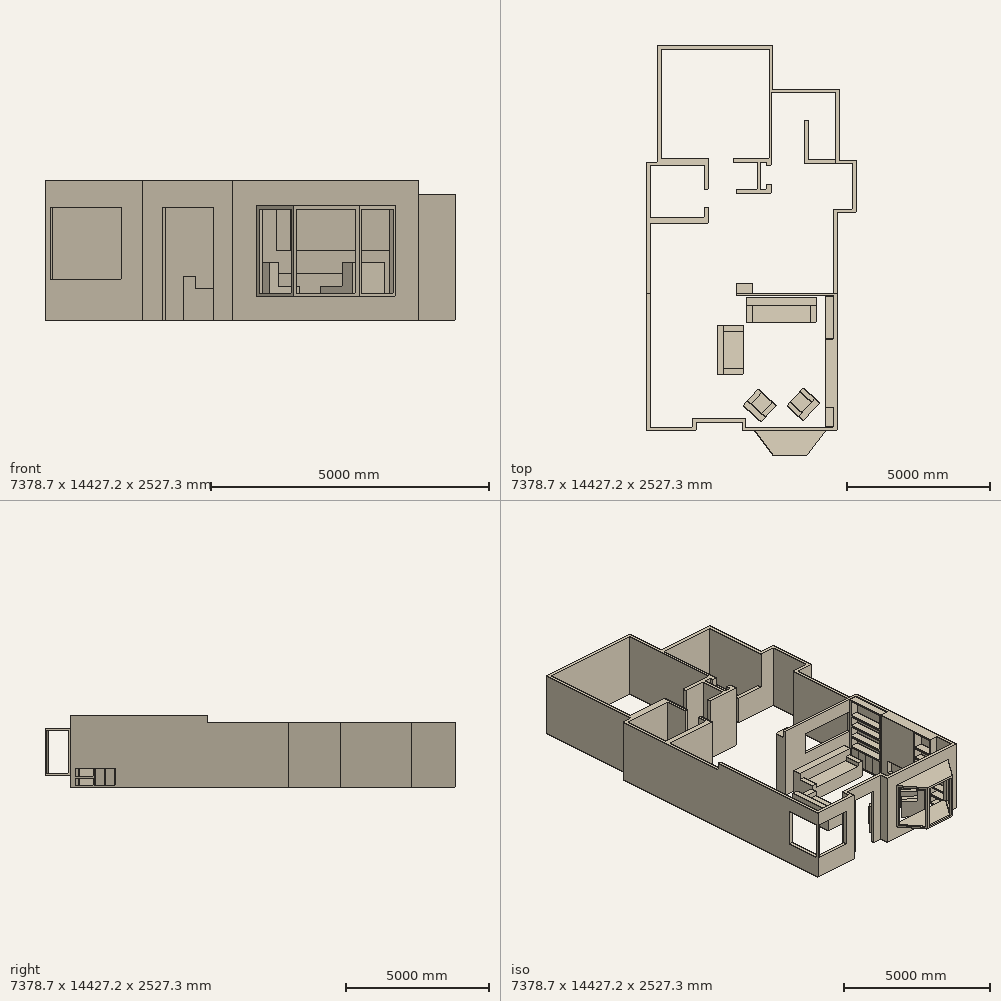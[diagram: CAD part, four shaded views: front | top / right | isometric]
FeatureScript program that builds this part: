
annotation { "Feature Type Name" : "Feature", "Feature Type Description" : "" }
export const myFeature = defineFeature(function(context is Context, id is Id, definition is map)
    precondition{}
    {
        {
            var Q0;
            Q0=qCreatedBy(makeId("Top.planeOp"),FACE);
            var sketch = newSketch(context, id + "F0", { "sketchPlane" : qUnion([Q0])});
            skLineSegment(sketch, "E0", {"start": v(6464.3, 0) * mm, "end": v(6464.3, 4622.8) * mm});
            skLineSegment(sketch, "E1", {"start": v(0, 0) * mm, "end": v(1498.6, 0) * mm});
            skLineSegment(sketch, "E2", {"start": v(1498.6, 0) * mm, "end": v(1498.6, 304.8) * mm});
            skLineSegment(sketch, "E3", {"start": v(1498.6, 304.8) * mm, "end": v(3359.15, 304.8) * mm});
            skLineSegment(sketch, "E4", {"start": v(3359.15, 304.8) * mm, "end": v(3359.15, 0) * mm});
            skLineSegment(sketch, "E5", {"start": v(3359.15, 0) * mm, "end": v(6464.3, 0) * mm});
            skLineSegment(sketch, "E6", {"start": v(6464.3, 4622.8) * mm, "end": v(3022.6, 4622.8) * mm});
            skLineSegment(sketch, "E7", {"start": v(3022.6, 4622.8) * mm, "end": v(3022.6, 5051.43) * mm});
            skLineSegment(sketch, "E8", {"start": v(3143.25, 5051.43) * mm, "end": v(3143.25, 5076.83) * mm});
            skLineSegment(sketch, "E9", {"start": v(3143.25, 5076.83) * mm, "end": v(3581.4, 5076.83) * mm});
            skLineSegment(sketch, "E10", {"start": v(3581.4, 5076.83) * mm, "end": v(3581.4, 4721.23) * mm});
            skLineSegment(sketch, "E11", {"start": v(3581.4, 4721.23) * mm, "end": v(6464.3, 4721.23) * mm});
            skLineSegment(sketch, "E12", {"start": v(6464.3, 4721.23) * mm, "end": v(6464.3, 7677.15) * mm});
            skLineSegment(sketch, "E13", {"start": v(0, 7175.5) * mm, "end": v(0, 0) * mm});
            skLineSegment(sketch, "E14", {"start": v(0, 7175.5) * mm, "end": v(2038.35, 7175.5) * mm});
            skLineSegment(sketch, "E15", {"start": v(2038.35, 7175.5) * mm, "end": v(2038.35, 7721.6) * mm});
            skLineSegment(sketch, "E16", {"start": v(2038.35, 7721.6) * mm, "end": v(1924.05, 7721.6) * mm});
            skLineSegment(sketch, "E17", {"start": v(1924.05, 7721.6) * mm, "end": v(1924.05, 7376.3) * mm});
            skLineSegment(sketch, "E18", {"start": v(1924.05, 7376.3) * mm, "end": v(0, 7376.3) * mm});
            skLineSegment(sketch, "E19", {"start": v(0, 7376.3) * mm, "end": v(0, 9205.1) * mm});
            skLineSegment(sketch, "E20", {"start": v(0, 9205.1) * mm, "end": v(1924.05, 9205.1) * mm});
            skLineSegment(sketch, "E21", {"start": v(1924.05, 9205.1) * mm, "end": v(1924.05, 8369.3) * mm});
            skLineSegment(sketch, "E22", {"start": v(1924.05, 8369.3) * mm, "end": v(2038.35, 8369.3) * mm});
            skLineSegment(sketch, "E23", {"start": v(2038.35, 8369.3) * mm, "end": v(2038.35, 9474.2) * mm});
            skLineSegment(sketch, "E24", {"start": v(6464.3, 7677.15) * mm, "end": v(7124.7, 7677.15) * mm});
            skLineSegment(sketch, "E25", {"start": v(7124.7, 7677.15) * mm, "end": v(7124.7, 9277.35) * mm});
            skLineSegment(sketch, "E26", {"start": v(7124.7, 9277.35) * mm, "end": v(5435.6, 9277.35) * mm});
            skLineSegment(sketch, "E27", {"start": v(5435.6, 9277.35) * mm, "end": v(5435.6, 10801.35) * mm});
            skLineSegment(sketch, "E28", {"start": v(5435.6, 10801.35) * mm, "end": v(5562.6, 10801.35) * mm});
            skLineSegment(sketch, "E29", {"start": v(5562.6, 10801.35) * mm, "end": v(5562.6, 9417.05) * mm});
            skLineSegment(sketch, "E30", {"start": v(5562.6, 9417.05) * mm, "end": v(6521.45, 9417.05) * mm});
            skLineSegment(sketch, "E31", {"start": v(6521.45, 9417.05) * mm, "end": v(6521.45, 11766.55) * mm});
            skLineSegment(sketch, "E32", {"start": v(6521.45, 11766.55) * mm, "end": v(4273.55, 11766.55) * mm});
            skLineSegment(sketch, "E33", {"start": v(4273.55, 11766.55) * mm, "end": v(4273.55, 9201.15) * mm});
            skLineSegment(sketch, "E34", {"start": v(4273.55, 9201.15) * mm, "end": v(4102.1, 9201.15) * mm});
            skLineSegment(sketch, "E35", {"start": v(4102.1, 9201.15) * mm, "end": v(4102.1, 9334.5) * mm});
            skLineSegment(sketch, "E36", {"start": v(4102.1, 9334.5) * mm, "end": v(3873.5, 9334.5) * mm});
            skLineSegment(sketch, "E37", {"start": v(3873.5, 9334.5) * mm, "end": v(3873.5, 8369.3) * mm});
            skLineSegment(sketch, "E38", {"start": v(3873.5, 8369.3) * mm, "end": v(4102.1, 8369.3) * mm});
            skLineSegment(sketch, "E39", {"start": v(4102.1, 8369.3) * mm, "end": v(4102.1, 8528.05) * mm});
            skLineSegment(sketch, "E40", {"start": v(4102.1, 8528.05) * mm, "end": v(4273.55, 8528.05) * mm});
            skLineSegment(sketch, "E41", {"start": v(4273.55, 8528.05) * mm, "end": v(4273.55, 8242.3) * mm});
            skLineSegment(sketch, "E42", {"start": v(4273.55, 8242.3) * mm, "end": v(3022.6, 8242.3) * mm});
            skLineSegment(sketch, "E43", {"start": v(3022.6, 8369.3) * mm, "end": v(3759.2, 8369.3) * mm});
            skLineSegment(sketch, "E44", {"start": v(3759.2, 8369.3) * mm, "end": v(3759.2, 9334.5) * mm});
            skLineSegment(sketch, "E45", {"start": v(3759.2, 9334.5) * mm, "end": v(2933.7, 9334.5) * mm});
            skLineSegment(sketch, "E46", {"start": v(2933.7, 9334.5) * mm, "end": v(2933.7, 9474.2) * mm});
            skLineSegment(sketch, "E47", {"start": v(2933.7, 9474.2) * mm, "end": v(4184.65, 9474.2) * mm});
            skLineSegment(sketch, "E48", {"start": v(4184.65, 9474.2) * mm, "end": v(4184.65, 13309.6) * mm});
            skLineSegment(sketch, "E49", {"start": v(4184.65, 13309.6) * mm, "end": v(387.35, 13309.6) * mm});
            skLineSegment(sketch, "E50", {"start": v(2038.35, 9474.2) * mm, "end": v(387.35, 9474.2) * mm});
            skLineSegment(sketch, "E51", {"start": v(387.35, 13309.6) * mm, "end": v(387.35, 9474.2) * mm});
            skLineSegment(sketch, "E52", {"start": v(260.35, 13436.6) * mm, "end": v(4311.65, 13436.6) * mm});
            skLineSegment(sketch, "E53", {"start": v(4311.65, 13436.6) * mm, "end": v(4311.65, 11893.55) * mm});
            skLineSegment(sketch, "E54", {"start": v(4311.65, 11893.55) * mm, "end": v(6648.45, 11893.55) * mm});
            skLineSegment(sketch, "E55", {"start": v(6648.45, 11893.55) * mm, "end": v(6648.45, 9404.35) * mm});
            skLineSegment(sketch, "E56", {"start": v(6648.45, 9404.35) * mm, "end": v(7251.7, 9404.35) * mm});
            skLineSegment(sketch, "E57", {"start": v(7251.7, 9404.35) * mm, "end": v(7251.7, 7550.15) * mm});
            skLineSegment(sketch, "E58", {"start": v(7251.7, 7550.15) * mm, "end": v(6591.3, 7550.15) * mm});
            skLineSegment(sketch, "E59", {"start": v(6591.3, 7550.15) * mm, "end": v(6591.3, -127) * mm});
            skLineSegment(sketch, "E60", {"start": v(6591.3, -127) * mm, "end": v(3232.15, -127) * mm});
            skLineSegment(sketch, "E61", {"start": v(3232.15, -127) * mm, "end": v(3232.15, 177.8) * mm});
            skLineSegment(sketch, "E62", {"start": v(3232.15, 177.8) * mm, "end": v(1625.6, 177.8) * mm});
            skLineSegment(sketch, "E63", {"start": v(1625.6, 177.8) * mm, "end": v(1625.6, -127) * mm});
            skLineSegment(sketch, "E64", {"start": v(1625.6, -127) * mm, "end": v(-127, -127) * mm});
            skLineSegment(sketch, "E65", {"start": v(-127, -127) * mm, "end": v(-127, 9332.1) * mm});
            skLineSegment(sketch, "E66", {"start": v(-127, 9332.1) * mm, "end": v(260.35, 9332.1) * mm});
            skLineSegment(sketch, "E67", {"start": v(260.35, 9332.1) * mm, "end": v(260.35, 13436.6) * mm});
            skLineSegment(sketch, "E68", {"start": v(3022.6, 8242.3) * mm, "end": v(3022.6, 8369.3) * mm});
            skLineSegment(sketch, "E69", {"start": v(3143.25, 5051.43) * mm, "end": v(3022.6, 5051.43) * mm});
            skLineSegment(sketch, "E70", {"start": v(4311.65, 11893.55) * mm, "end": v(387.35, 11893.55) * mm, "construction": true});
            skLineSegment(sketch, "E71", {"start": v(5435.6, 10801.35) * mm, "end": v(4311.65, 10801.35) * mm, "construction": true});
            skLineSegment(sketch, "E72", {"start": v(5435.6, 10604.3) * mm, "end": v(4273.55, 10604.3) * mm, "construction": true});
            skLineSegment(sketch, "E73", {"start": v(5435.6, 10801.35) * mm, "end": v(5435.6, 11766.55) * mm, "construction": true});
            skLineSegment(sketch, "E74", {"start": v(5562.6, 10801.35) * mm, "end": v(5697.75, 10801.35) * mm, "construction": true});
            skLineSegment(sketch, "E75", {"start": v(5697.75, 10801.35) * mm, "end": v(5697.75, 11766.55) * mm, "construction": true});
            skLineSegment(sketch, "E76", {"start": v(5562.6, 10552.21) * mm, "end": v(6521.45, 10552.21) * mm, "construction": true});
            skLineSegment(sketch, "E77", {"start": v(5697.75, 10801.35) * mm, "end": v(6521.45, 10801.35) * mm, "construction": true});
            skLineSegment(sketch, "E78", {"start": v(5562.6, 10248.4) * mm, "end": v(6521.45, 10248.4) * mm, "construction": true});
            skLineSegment(sketch, "E79", {"start": v(5562.6, 9918.56) * mm, "end": v(6521.45, 9918.56) * mm, "construction": true});
            skLineSegment(sketch, "E80", {"start": v(5562.6, 9649.48) * mm, "end": v(6521.45, 9649.48) * mm, "construction": true});
            skLineSegment(sketch, "E81", {"start": v(3022.6, 5051.43) * mm, "end": v(3022.6, 9334.5) * mm, "construction": true});
            skSolve(sketch);
        }
        {
            var Q0;
            Q0 = qSketchRegion(id + "F0", true);
            extrude(context, id + "F1", {"entities" : qUnion([Q0]), "depth" : 2527.3 * mm, "offsetDistance" : 25.4 * mm});
        }
        {
            var Q0;
            Q0=qCreatedBy(makeId("Top.planeOp"),FACE);
            cPlane(context, id + "F2", {"entities" : qUnion([Q0]), "cplaneType" : CPlaneType.OFFSET, "offset" : 2527.3 * mm, "width" : 152.4 * mm, "height" : 152.4 * mm});
        }
        {
            var Q0;
            Q0=qCreatedBy(id+"F2.planeOp",FACE);
            var sketch = newSketch(context, id + "F3", { "sketchPlane" : qUnion([Q0])});
            skLineSegment(sketch, "E82.bottom", {"start": v(7612.4, 4721.23) * mm, "end": v(-1331.12, 4721.23) * mm});
            skLineSegment(sketch, "E82.top", {"start": v(7612.4, 14060.6) * mm, "end": v(-1331.12, 14060.6) * mm});
            skLineSegment(sketch, "E82.left", {"start": v(7612.4, 4721.23) * mm, "end": v(7612.4, 14060.6) * mm});
            skLineSegment(sketch, "E82.right", {"start": v(-1331.12, 4721.23) * mm, "end": v(-1331.12, 14060.6) * mm});
            skSolve(sketch);
        }
        {
            var Q0;
            Q0 = qSketchRegion(id + "F3", true);
            extrude(context, id + "F4", {"entities" : qUnion([Q0]), "operationType" : NewBodyOperationType.REMOVE, "oppositeDirection" : true, "depth" : 254 * mm, "offsetDistance" : 25.4 * mm});
        }
        {
            var Q0;
            Q0=qCreatedBy(id+"F2.planeOp",FACE);
            var sketch = newSketch(context, id + "F5", { "sketchPlane" : qUnion([Q0])});
            skLineSegment(sketch, "E83.bottom", {"start": v(5253.25, 10968.73) * mm, "end": v(6521.45, 10968.73) * mm});
            skLineSegment(sketch, "E83.top", {"start": v(5253.25, 9146.6) * mm, "end": v(6521.45, 9146.6) * mm});
            skLineSegment(sketch, "E83.left", {"start": v(5253.25, 10968.73) * mm, "end": v(5253.25, 9146.6) * mm});
            skLineSegment(sketch, "E83.right", {"start": v(6521.45, 10968.73) * mm, "end": v(6521.45, 9146.6) * mm});
            skSolve(sketch);
        }
        {
            var Q0;
            Q0 = qSketchRegion(id + "F5", true);
            extrude(context, id + "F6", {"entities" : qUnion([Q0]), "operationType" : NewBodyOperationType.REMOVE, "oppositeDirection" : true, "depth" : 1562.1 * mm, "offsetDistance" : 25.4 * mm});
        }
        {
            var Q0;
            Q0=qCreatedBy(makeId("Top.planeOp"),FACE);
            var sketch = newSketch(context, id + "F7", { "sketchPlane" : qUnion([Q0])});
            skLineSegment(sketch, "E84", {"start": v(6464.3, 3098.8) * mm, "end": v(6159.5, 3098.8) * mm});
            skLineSegment(sketch, "E85", {"start": v(6159.5, 3098.8) * mm, "end": v(6159.5, 1524) * mm});
            skLineSegment(sketch, "E86", {"start": v(6159.5, 1524) * mm, "end": v(6464.3, 1524) * mm});
            skLineSegment(sketch, "E87", {"start": v(6464.3, 3098.8) * mm, "end": v(6464.3, 1524) * mm});
            skSolve(sketch);
        }
        {
            var Q0;
            Q0 = qSketchRegion(id + "F7", true);
            var Q1;
            Q1=makeQuery(id+"F1.opExtrude","CAP_FACE",FACE,{"disambiguationData":[OSD([sQuery(id+"F0.wireOp",EDGE,"E0"),sQuery(id+"F0.wireOp",EDGE,"E1"),sQuery(id+"F0.wireOp",EDGE,"E2"),sQuery(id+"F0.wireOp",EDGE,"E3"),sQuery(id+"F0.wireOp",EDGE,"E4"),sQuery(id+"F0.wireOp",EDGE,"E5"),sQuery(id+"F0.wireOp",EDGE,"E6"),sQuery(id+"F0.wireOp",EDGE,"E7"),sQuery(id+"F0.wireOp",EDGE,"E8"),sQuery(id+"F0.wireOp",EDGE,"E9"),sQuery(id+"F0.wireOp",EDGE,"E10"),sQuery(id+"F0.wireOp",EDGE,"E11"),sQuery(id+"F0.wireOp",EDGE,"E12"),sQuery(id+"F0.wireOp",EDGE,"E13"),sQuery(id+"F0.wireOp",EDGE,"E14"),sQuery(id+"F0.wireOp",EDGE,"E15"),sQuery(id+"F0.wireOp",EDGE,"E16"),sQuery(id+"F0.wireOp",EDGE,"E17"),sQuery(id+"F0.wireOp",EDGE,"E18"),sQuery(id+"F0.wireOp",EDGE,"E19"),sQuery(id+"F0.wireOp",EDGE,"E20"),sQuery(id+"F0.wireOp",EDGE,"E21"),sQuery(id+"F0.wireOp",EDGE,"E22"),sQuery(id+"F0.wireOp",EDGE,"E23"),sQuery(id+"F0.wireOp",EDGE,"E24"),sQuery(id+"F0.wireOp",EDGE,"E25"),sQuery(id+"F0.wireOp",EDGE,"E26"),sQuery(id+"F0.wireOp",EDGE,"E27"),sQuery(id+"F0.wireOp",EDGE,"E28"),sQuery(id+"F0.wireOp",EDGE,"E29"),sQuery(id+"F0.wireOp",EDGE,"E30"),sQuery(id+"F0.wireOp",EDGE,"E31"),sQuery(id+"F0.wireOp",EDGE,"E32"),sQuery(id+"F0.wireOp",EDGE,"E33"),sQuery(id+"F0.wireOp",EDGE,"E34"),sQuery(id+"F0.wireOp",EDGE,"E35"),sQuery(id+"F0.wireOp",EDGE,"E36"),sQuery(id+"F0.wireOp",EDGE,"E37"),sQuery(id+"F0.wireOp",EDGE,"E38"),sQuery(id+"F0.wireOp",EDGE,"E39"),sQuery(id+"F0.wireOp",EDGE,"E40"),sQuery(id+"F0.wireOp",EDGE,"E41"),sQuery(id+"F0.wireOp",EDGE,"E42"),sQuery(id+"F0.wireOp",EDGE,"E43"),sQuery(id+"F0.wireOp",EDGE,"E44"),sQuery(id+"F0.wireOp",EDGE,"E45"),sQuery(id+"F0.wireOp",EDGE,"E46"),sQuery(id+"F0.wireOp",EDGE,"E47"),sQuery(id+"F0.wireOp",EDGE,"E48"),sQuery(id+"F0.wireOp",EDGE,"E49"),sQuery(id+"F0.wireOp",EDGE,"E50"),sQuery(id+"F0.wireOp",EDGE,"E51"),sQuery(id+"F0.wireOp",EDGE,"E52"),sQuery(id+"F0.wireOp",EDGE,"E53"),sQuery(id+"F0.wireOp",EDGE,"E54"),sQuery(id+"F0.wireOp",EDGE,"E55"),sQuery(id+"F0.wireOp",EDGE,"E56"),sQuery(id+"F0.wireOp",EDGE,"E57"),sQuery(id+"F0.wireOp",EDGE,"E58"),sQuery(id+"F0.wireOp",EDGE,"E59"),sQuery(id+"F0.wireOp",EDGE,"E60"),sQuery(id+"F0.wireOp",EDGE,"E61"),sQuery(id+"F0.wireOp",EDGE,"E62"),sQuery(id+"F0.wireOp",EDGE,"E63"),sQuery(id+"F0.wireOp",EDGE,"E64"),sQuery(id+"F0.wireOp",EDGE,"E65"),sQuery(id+"F0.wireOp",EDGE,"E66"),sQuery(id+"F0.wireOp",EDGE,"E67"),sQuery(id+"F0.wireOp",EDGE,"E68"),sQuery(id+"F0.wireOp",EDGE,"E69")])],"isStart":false});
            extrude(context, id + "F8", {"entities" : qUnion([Q0]), "operationType" : NewBodyOperationType.ADD, "depth" : 2527.3 * mm, "endBoundEntityFace" : qUnion([Q1]), "offsetDistance" : 25.4 * mm});
        }
        {
            var Q0;
            Q0=makeQuery(id+"F8.opExtrude","SWEPT_FACE",FACE,{"disambiguationData":[OSD([sQuery(id+"F7.wireOp",EDGE,"E85")])]});
            var sketch = newSketch(context, id + "F9", { "sketchPlane" : qUnion([Q0])});
            skLineSegment(sketch, "E88.bottom", {"start": v(-1854.2, 381) * mm, "end": v(-2768.6, 381) * mm});
            skLineSegment(sketch, "E88.top", {"start": v(-1854.2, 838.2) * mm, "end": v(-2768.6, 838.2) * mm});
            skLineSegment(sketch, "E88.left", {"start": v(-1854.2, 381) * mm, "end": v(-1854.2, 838.2) * mm});
            skLineSegment(sketch, "E88.right", {"start": v(-2768.6, 381) * mm, "end": v(-2768.6, 838.2) * mm});
            skPoint(sketch, "E88.middle", {"position": v(-2311.4, 609.6) * mm});
            skSolve(sketch);
        }
        {
            var Q0;
            Q0 = qSketchRegion(id + "F9", true);
            extrude(context, id + "F10", {"entities" : qUnion([Q0]), "operationType" : NewBodyOperationType.REMOVE, "oppositeDirection" : true, "depth" : 152.4 * mm, "offsetDistance" : 25.4 * mm});
        }
        {
            var Q0;
            Q0=makeQuery(id+"F1.opExtrude","SWEPT_FACE",FACE,{"disambiguationData":[OSD([sQuery(id+"F0.wireOp",EDGE,"E60")])]});
            var sketch = newSketch(context, id + "F11", { "sketchPlane" : qUnion([Q0])});
            skLineSegment(sketch, "E89.bottom", {"start": v(3771.9, 2044.7) * mm, "end": v(6083.3, 2044.7) * mm});
            skLineSegment(sketch, "E89.top", {"start": v(3771.9, 457.2) * mm, "end": v(6083.3, 457.2) * mm});
            skLineSegment(sketch, "E89.left", {"start": v(3771.9, 2044.7) * mm, "end": v(3771.9, 457.2) * mm});
            skLineSegment(sketch, "E89.right", {"start": v(6083.3, 2044.7) * mm, "end": v(6083.3, 457.2) * mm});
            skSolve(sketch);
        }
        {
            var Q0;
            Q0 = qSketchRegion(id + "F11", true);
            extrude(context, id + "F12", {"entities" : qUnion([Q0]), "operationType" : NewBodyOperationType.REMOVE, "endBound" : BoundingType.UP_TO_NEXT, "oppositeDirection" : true, "depth" : 25.4 * mm, "offsetDistance" : 25.4 * mm});
        }
        {
            var Q0;
            Q0=makeQuery(id+"F12.boolean.opBoolean","COPY",FACE,{"derivedFrom":makeQuery(id+"F12.opExtrude","SWEPT_FACE",FACE,{"disambiguationData":[OSD([sQuery(id+"F11.wireOp",EDGE,"E89.top")])]})});
            var sketch = newSketch(context, id + "F13", { "sketchPlane" : qUnion([Q0])});
            skLineSegment(sketch, "E90.bottom", {"start": v(5486.4, -914.4) * mm, "end": v(4368.8, -914.4) * mm});
            skPoint(sketch, "E90.middle", {"position": v(4927.6, -520.7) * mm});
            skPoint(sketch, "E91", {"position": v(4368.8, -914.4) * mm});
            skPoint(sketch, "E92", {"position": v(5486.4, -914.4) * mm});
            skLineSegment(sketch, "E93", {"start": v(3771.9, -127) * mm, "end": v(4368.8, -914.4) * mm});
            skLineSegment(sketch, "E94", {"start": v(5486.4, -914.4) * mm, "end": v(6083.3, -127) * mm});
            skLineSegment(sketch, "E95.0", {"start": v(5524.26, -990.6) * mm, "end": v(6178.92, -127) * mm});
            skLineSegment(sketch, "E95.1", {"start": v(5524.26, -990.6) * mm, "end": v(4330.94, -990.6) * mm});
            skLineSegment(sketch, "E95.2", {"start": v(3676.28, -127) * mm, "end": v(4330.94, -990.6) * mm});
            skLineSegment(sketch, "E96", {"start": v(3771.9, -127) * mm, "end": v(3676.28, -127) * mm});
            skLineSegment(sketch, "E97", {"start": v(6083.3, -127) * mm, "end": v(6178.92, -127) * mm});
            skSolve(sketch);
        }
        {
            var Q0;
            Q0 = qSketchRegion(id + "F13", true);
            var Q1;
            Q1=makeQuery(id+"F12.boolean.opBoolean","COPY",FACE,{"derivedFrom":makeQuery(id+"F12.opExtrude","SWEPT_FACE",FACE,{"disambiguationData":[OSD([sQuery(id+"F11.wireOp",EDGE,"E89.bottom")])]})});
            extrude(context, id + "F14", {"entities" : qUnion([Q0]), "operationType" : NewBodyOperationType.ADD, "endBound" : BoundingType.UP_TO_SURFACE, "depth" : 1546.86 * mm, "endBoundEntityFace" : qUnion([Q1]), "offsetDistance" : 25.4 * mm});
        }
        {
            var Q0;
            Q0=makeQuery(id+"F14.opExtrude","CAP_FACE",FACE,{"disambiguationData":[OSD([sQuery(id+"F13.wireOp",EDGE,"E90.bottom"),sQuery(id+"F13.wireOp",EDGE,"E93"),sQuery(id+"F13.wireOp",EDGE,"E94"),sQuery(id+"F13.wireOp",EDGE,"E95.0"),sQuery(id+"F13.wireOp",EDGE,"E95.1"),sQuery(id+"F13.wireOp",EDGE,"E95.2"),sQuery(id+"F13.wireOp",EDGE,"E96"),sQuery(id+"F13.wireOp",EDGE,"E97")])],"isStart":false});
            var sketch = newSketch(context, id + "F15", { "sketchPlane" : qUnion([Q0])});
            skLineSegment(sketch, "E98", {"start": v(3676.28, -127) * mm, "end": v(4330.94, -990.6) * mm});
            skLineSegment(sketch, "E99", {"start": v(4330.94, -990.6) * mm, "end": v(5524.26, -990.6) * mm});
            skLineSegment(sketch, "E100", {"start": v(5524.26, -990.6) * mm, "end": v(6178.92, -127) * mm});
            skLineSegment(sketch, "E101", {"start": v(6178.92, -127) * mm, "end": v(3676.28, -127) * mm});
            skSolve(sketch);
        }
        {
            var Q0;
            Q0 = qSketchRegion(id + "F15", true);
            extrude(context, id + "F16", {"entities" : qUnion([Q0]), "operationType" : NewBodyOperationType.ADD, "depth" : 25.4 * mm, "offsetDistance" : 25.4 * mm});
        }
        {
            var Q0;
            Q0=makeQuery(id+"F14.opExtrude","CAP_FACE",FACE,{"disambiguationData":[OSD([sQuery(id+"F13.wireOp",EDGE,"E90.bottom"),sQuery(id+"F13.wireOp",EDGE,"E93"),sQuery(id+"F13.wireOp",EDGE,"E94"),sQuery(id+"F13.wireOp",EDGE,"E95.0"),sQuery(id+"F13.wireOp",EDGE,"E95.1"),sQuery(id+"F13.wireOp",EDGE,"E95.2"),sQuery(id+"F13.wireOp",EDGE,"E96"),sQuery(id+"F13.wireOp",EDGE,"E97")])],"isStart":true});
            var sketch = newSketch(context, id + "F17", { "sketchPlane" : qUnion([Q0])});
            skLineSegment(sketch, "E102", {"start": v(3676.28, 127) * mm, "end": v(4330.94, 990.6) * mm});
            skLineSegment(sketch, "E103", {"start": v(4330.94, 990.6) * mm, "end": v(5524.26, 990.6) * mm});
            skLineSegment(sketch, "E104", {"start": v(5524.26, 990.6) * mm, "end": v(6178.92, 127) * mm});
            skLineSegment(sketch, "E105", {"start": v(6178.92, 127) * mm, "end": v(3676.28, 127) * mm});
            skSolve(sketch);
        }
        {
            var Q0;
            Q0 = qSketchRegion(id + "F17", true);
            extrude(context, id + "F18", {"entities" : qUnion([Q0]), "operationType" : NewBodyOperationType.ADD, "depth" : 25.4 * mm, "offsetDistance" : 25.4 * mm});
        }
        {
            var Q0;
            Q0=makeQuery(id+"F14.opExtrude","SWEPT_FACE",FACE,{"disambiguationData":[OSD([sQuery(id+"F13.wireOp",EDGE,"E90.bottom")])]});
            var sketch = newSketch(context, id + "F19", { "sketchPlane" : qUnion([Q0])});
            skLineSegment(sketch, "E106.bottom", {"start": v(-4394.2, 495.3) * mm, "end": v(-5461, 495.3) * mm});
            skLineSegment(sketch, "E106.top", {"start": v(-4394.2, 1993.9) * mm, "end": v(-5461, 1993.9) * mm});
            skLineSegment(sketch, "E106.left", {"start": v(-4394.2, 495.3) * mm, "end": v(-4394.2, 1993.9) * mm});
            skLineSegment(sketch, "E106.right", {"start": v(-5461, 495.3) * mm, "end": v(-5461, 1993.9) * mm});
            skPoint(sketch, "E106.middle", {"position": v(-4927.6, 1244.6) * mm});
            skSolve(sketch);
        }
        {
            var Q0;
            Q0 = qSketchRegion(id + "F19", true);
            extrude(context, id + "F20", {"entities" : qUnion([Q0]), "operationType" : NewBodyOperationType.REMOVE, "endBound" : BoundingType.UP_TO_NEXT, "oppositeDirection" : true, "depth" : 25.4 * mm, "offsetDistance" : 25.4 * mm});
        }
        {
            var Q0;
            Q0=makeQuery(id+"F14.opExtrude","SWEPT_FACE",FACE,{"disambiguationData":[OSD([sQuery(id+"F13.wireOp",EDGE,"E93")])]});
            var sketch = newSketch(context, id + "F21", { "sketchPlane" : qUnion([Q0])});
            skLineSegment(sketch, "E107.bottom", {"start": v(-3342.5, 1993.9) * mm, "end": v(-2405.23, 1993.9) * mm});
            skLineSegment(sketch, "E107.top", {"start": v(-3342.5, 495.3) * mm, "end": v(-2405.23, 495.3) * mm});
            skLineSegment(sketch, "E107.left", {"start": v(-3342.5, 1993.9) * mm, "end": v(-3342.5, 495.3) * mm});
            skLineSegment(sketch, "E107.right", {"start": v(-2405.23, 1993.9) * mm, "end": v(-2405.23, 495.3) * mm});
            skSolve(sketch);
        }
        {
            var Q0;
            Q0 = qSketchRegion(id + "F21", true);
            extrude(context, id + "F22", {"entities" : qUnion([Q0]), "operationType" : NewBodyOperationType.REMOVE, "endBound" : BoundingType.UP_TO_NEXT, "oppositeDirection" : true, "depth" : 25.4 * mm, "offsetDistance" : 25.4 * mm});
        }
        {
            var Q0;
            Q0=makeQuery(id+"F14.opExtrude","SWEPT_FACE",FACE,{"disambiguationData":[OSD([sQuery(id+"F13.wireOp",EDGE,"E94")])]});
            var sketch = newSketch(context, id + "F23", { "sketchPlane" : qUnion([Q0])});
            skLineSegment(sketch, "E108.bottom", {"start": v(-3548.35, 1993.9) * mm, "end": v(-2611.07, 1993.9) * mm});
            skLineSegment(sketch, "E108.top", {"start": v(-3548.35, 495.3) * mm, "end": v(-2611.07, 495.3) * mm});
            skLineSegment(sketch, "E108.left", {"start": v(-3548.35, 1993.9) * mm, "end": v(-3548.35, 495.3) * mm});
            skLineSegment(sketch, "E108.right", {"start": v(-2611.07, 1993.9) * mm, "end": v(-2611.07, 495.3) * mm});
            skSolve(sketch);
        }
        {
            var Q0;
            Q0 = qSketchRegion(id + "F23", true);
            extrude(context, id + "F24", {"entities" : qUnion([Q0]), "operationType" : NewBodyOperationType.REMOVE, "endBound" : BoundingType.UP_TO_NEXT, "oppositeDirection" : true, "depth" : 25.4 * mm, "offsetDistance" : 25.4 * mm});
        }
        {
            var Q0;
            Q0=makeQuery(id+"F1.opExtrude","SWEPT_FACE",FACE,{"disambiguationData":[OSD([sQuery(id+"F0.wireOp",EDGE,"E3")])]});
            var sketch = newSketch(context, id + "F25", { "sketchPlane" : qUnion([Q0])});
            skLineSegment(sketch, "E109.bottom", {"start": v(-2889.25, 2032) * mm, "end": v(-1987.55, 2032) * mm});
            skLineSegment(sketch, "E109.top", {"start": v(-2889.25, 0) * mm, "end": v(-1987.55, 0) * mm});
            skLineSegment(sketch, "E109.left", {"start": v(-2889.25, 2032) * mm, "end": v(-2889.25, 0) * mm});
            skLineSegment(sketch, "E109.right", {"start": v(-1987.55, 2032) * mm, "end": v(-1987.55, 0) * mm});
            skSolve(sketch);
        }
        {
            var Q0;
            Q0 = qSketchRegion(id + "F25", true);
            extrude(context, id + "F26", {"entities" : qUnion([Q0]), "operationType" : NewBodyOperationType.REMOVE, "endBound" : BoundingType.UP_TO_NEXT, "oppositeDirection" : true, "depth" : 25.4 * mm, "offsetDistance" : 25.4 * mm});
        }
        {
            var Q0;
            Q0=makeQuery(id+"F1.opExtrude","SWEPT_FACE",FACE,{"disambiguationData":[OSD([sQuery(id+"F0.wireOp",EDGE,"E1")])]});
            var sketch = newSketch(context, id + "F27", { "sketchPlane" : qUnion([Q0])});
            skLineSegment(sketch, "E110.bottom", {"start": v(-1244.6, 2032) * mm, "end": v(38.1, 2032) * mm});
            skLineSegment(sketch, "E110.top", {"start": v(-1244.6, 749.3) * mm, "end": v(38.1, 749.3) * mm});
            skLineSegment(sketch, "E110.left", {"start": v(-1244.6, 2032) * mm, "end": v(-1244.6, 749.3) * mm});
            skLineSegment(sketch, "E110.right", {"start": v(38.1, 2032) * mm, "end": v(38.1, 749.3) * mm});
            skSolve(sketch);
        }
        {
            var Q0;
            Q0 = qSketchRegion(id + "F27", true);
            extrude(context, id + "F28", {"entities" : qUnion([Q0]), "operationType" : NewBodyOperationType.REMOVE, "endBound" : BoundingType.UP_TO_NEXT, "oppositeDirection" : true, "depth" : 25.4 * mm, "offsetDistance" : 25.4 * mm});
        }
        {
            var Q0;
            Q0=makeQuery(id+"F1.opExtrude","SWEPT_FACE",FACE,{"disambiguationData":[OSD([sQuery(id+"F0.wireOp",EDGE,"E13")])]});
            var sketch = newSketch(context, id + "F29", { "sketchPlane" : qUnion([Q0])});
            skLineSegment(sketch, "E111.bottom", {"start": v(-31.75, 2032) * mm, "end": v(1250.95, 2032) * mm});
            skLineSegment(sketch, "E111.top", {"start": v(-31.75, 749.3) * mm, "end": v(1250.95, 749.3) * mm});
            skLineSegment(sketch, "E111.left", {"start": v(-31.75, 2032) * mm, "end": v(-31.75, 749.3) * mm});
            skLineSegment(sketch, "E111.right", {"start": v(1250.95, 2032) * mm, "end": v(1250.95, 749.3) * mm});
            skSolve(sketch);
        }
        {
            var Q0;
            Q0 = qSketchRegion(id + "F29", true);
            extrude(context, id + "F30", {"entities" : qUnion([Q0]), "operationType" : NewBodyOperationType.REMOVE, "endBound" : BoundingType.UP_TO_NEXT, "oppositeDirection" : true, "depth" : 25.4 * mm, "offsetDistance" : 25.4 * mm});
        }
        {
            var Q0;
            Q0=makeQuery(id+"F30.boolean.opBoolean","INTERSECT",EDGE,{"derivedFrom":[makeQuery(id+"F28.boolean.opBoolean","COPY",FACE,{"derivedFrom":makeQuery(id+"F28.opExtrude","SWEPT_FACE",FACE,{"disambiguationData":[OSD([sQuery(id+"F27.wireOp",EDGE,"E110.right")])]})}),makeQuery(id+"F30.opExtrude","SWEPT_FACE",FACE,{"disambiguationData":[OSD([sQuery(id+"F29.wireOp",EDGE,"E111.left")])]})]});
            chamfer(context, id + "F31", {"entities" : qUnion([Q0]), "width" : 43.18 * mm, "tangentPropagation" : true});
        }
        {
            var Q0;
            Q0=qCreatedBy(makeId("Top.planeOp"),FACE);
            var sketch = newSketch(context, id + "F32", { "sketchPlane" : qUnion([Q0])});
            skLineSegment(sketch, "E112.bottom", {"start": v(6159.5, 4610.1) * mm, "end": v(6451.6, 4610.1) * mm});
            skLineSegment(sketch, "E112.top", {"start": v(6159.5, 3111.5) * mm, "end": v(6451.6, 3111.5) * mm});
            skLineSegment(sketch, "E112.left", {"start": v(6159.5, 4610.1) * mm, "end": v(6159.5, 3111.5) * mm});
            skLineSegment(sketch, "E112.right", {"start": v(6451.6, 4610.1) * mm, "end": v(6451.6, 3111.5) * mm});
            skSolve(sketch);
        }
        {
            var Q0;
            Q0 = qSketchRegion(id + "F32", true);
            var Q1;
            Q1=makeQuery(id+"F8.boolean.opBoolean","MERGE",FACE,{"derivedFrom":[makeQuery(id+"F1.opExtrude","CAP_FACE",FACE,{"disambiguationData":[OSD([sQuery(id+"F0.wireOp",EDGE,"E0"),sQuery(id+"F0.wireOp",EDGE,"E1"),sQuery(id+"F0.wireOp",EDGE,"E2"),sQuery(id+"F0.wireOp",EDGE,"E3"),sQuery(id+"F0.wireOp",EDGE,"E4"),sQuery(id+"F0.wireOp",EDGE,"E5"),sQuery(id+"F0.wireOp",EDGE,"E6"),sQuery(id+"F0.wireOp",EDGE,"E7"),sQuery(id+"F0.wireOp",EDGE,"E8"),sQuery(id+"F0.wireOp",EDGE,"E9"),sQuery(id+"F0.wireOp",EDGE,"E10"),sQuery(id+"F0.wireOp",EDGE,"E11"),sQuery(id+"F0.wireOp",EDGE,"E12"),sQuery(id+"F0.wireOp",EDGE,"E13"),sQuery(id+"F0.wireOp",EDGE,"E14"),sQuery(id+"F0.wireOp",EDGE,"E15"),sQuery(id+"F0.wireOp",EDGE,"E16"),sQuery(id+"F0.wireOp",EDGE,"E17"),sQuery(id+"F0.wireOp",EDGE,"E18"),sQuery(id+"F0.wireOp",EDGE,"E19"),sQuery(id+"F0.wireOp",EDGE,"E20"),sQuery(id+"F0.wireOp",EDGE,"E21"),sQuery(id+"F0.wireOp",EDGE,"E22"),sQuery(id+"F0.wireOp",EDGE,"E23"),sQuery(id+"F0.wireOp",EDGE,"E24"),sQuery(id+"F0.wireOp",EDGE,"E25"),sQuery(id+"F0.wireOp",EDGE,"E26"),sQuery(id+"F0.wireOp",EDGE,"E27"),sQuery(id+"F0.wireOp",EDGE,"E28"),sQuery(id+"F0.wireOp",EDGE,"E29"),sQuery(id+"F0.wireOp",EDGE,"E30"),sQuery(id+"F0.wireOp",EDGE,"E31"),sQuery(id+"F0.wireOp",EDGE,"E32"),sQuery(id+"F0.wireOp",EDGE,"E33"),sQuery(id+"F0.wireOp",EDGE,"E34"),sQuery(id+"F0.wireOp",EDGE,"E35"),sQuery(id+"F0.wireOp",EDGE,"E36"),sQuery(id+"F0.wireOp",EDGE,"E37"),sQuery(id+"F0.wireOp",EDGE,"E38"),sQuery(id+"F0.wireOp",EDGE,"E39"),sQuery(id+"F0.wireOp",EDGE,"E40"),sQuery(id+"F0.wireOp",EDGE,"E41"),sQuery(id+"F0.wireOp",EDGE,"E42"),sQuery(id+"F0.wireOp",EDGE,"E43"),sQuery(id+"F0.wireOp",EDGE,"E44"),sQuery(id+"F0.wireOp",EDGE,"E45"),sQuery(id+"F0.wireOp",EDGE,"E46"),sQuery(id+"F0.wireOp",EDGE,"E47"),sQuery(id+"F0.wireOp",EDGE,"E48"),sQuery(id+"F0.wireOp",EDGE,"E49"),sQuery(id+"F0.wireOp",EDGE,"E50"),sQuery(id+"F0.wireOp",EDGE,"E51"),sQuery(id+"F0.wireOp",EDGE,"E52"),sQuery(id+"F0.wireOp",EDGE,"E53"),sQuery(id+"F0.wireOp",EDGE,"E54"),sQuery(id+"F0.wireOp",EDGE,"E55"),sQuery(id+"F0.wireOp",EDGE,"E56"),sQuery(id+"F0.wireOp",EDGE,"E57"),sQuery(id+"F0.wireOp",EDGE,"E58"),sQuery(id+"F0.wireOp",EDGE,"E59"),sQuery(id+"F0.wireOp",EDGE,"E60"),sQuery(id+"F0.wireOp",EDGE,"E61"),sQuery(id+"F0.wireOp",EDGE,"E62"),sQuery(id+"F0.wireOp",EDGE,"E63"),sQuery(id+"F0.wireOp",EDGE,"E64"),sQuery(id+"F0.wireOp",EDGE,"E65"),sQuery(id+"F0.wireOp",EDGE,"E66"),sQuery(id+"F0.wireOp",EDGE,"E67"),sQuery(id+"F0.wireOp",EDGE,"E68"),sQuery(id+"F0.wireOp",EDGE,"E69")])],"isStart":false}),makeQuery(id+"F8.opExtrude","CAP_FACE",FACE,{"disambiguationData":[OSD([sQuery(id+"F7.wireOp",EDGE,"E84"),sQuery(id+"F7.wireOp",EDGE,"E85"),sQuery(id+"F7.wireOp",EDGE,"E86"),sQuery(id+"F7.wireOp",EDGE,"E87")])],"isStart":false})]});
            extrude(context, id + "F33", {"entities" : qUnion([Q0]), "endBound" : BoundingType.UP_TO_SURFACE, "depth" : 25.4 * mm, "endBoundEntityFace" : qUnion([Q1]), "offsetDistance" : 25.4 * mm});
        }
        {
            var Q0;
            Q0=makeQuery(id+"F33.opExtrude","SWEPT_FACE",FACE,{"disambiguationData":[OSD([sQuery(id+"F32.wireOp",EDGE,"E112.left")])]});
            var sketch = newSketch(context, id + "F34", { "sketchPlane" : qUnion([Q0])});
            skLineSegment(sketch, "E113.bottom", {"start": v(-4559.3, 660.4) * mm, "end": v(-4210.05, 660.4) * mm});
            skLineSegment(sketch, "E113.top", {"start": v(-4559.3, 50.8) * mm, "end": v(-4210.05, 50.8) * mm});
            skLineSegment(sketch, "E113.left", {"start": v(-4559.3, 660.4) * mm, "end": v(-4559.3, 50.8) * mm});
            skLineSegment(sketch, "E113.right", {"start": v(-4210.05, 660.4) * mm, "end": v(-4210.05, 50.8) * mm});
            skLineSegment(sketch, "E114.1.0.0", {"start": v(-3860.8, 660.4) * mm, "end": v(-3860.8, 50.8) * mm});
            skLineSegment(sketch, "E114.1.0.1", {"start": v(-4210.05, 50.8) * mm, "end": v(-3860.8, 50.8) * mm});
            skLineSegment(sketch, "E114.1.0.3", {"start": v(-4210.05, 660.4) * mm, "end": v(-3860.8, 660.4) * mm});
            skLineSegment(sketch, "E114.2.0.0", {"start": v(-3511.55, 660.4) * mm, "end": v(-3511.55, 50.8) * mm});
            skLineSegment(sketch, "E114.2.0.1", {"start": v(-3860.8, 50.8) * mm, "end": v(-3511.55, 50.8) * mm});
            skLineSegment(sketch, "E114.2.0.2", {"start": v(-3860.8, 660.4) * mm, "end": v(-3860.8, 50.8) * mm});
            skLineSegment(sketch, "E114.2.0.3", {"start": v(-3860.8, 660.4) * mm, "end": v(-3511.55, 660.4) * mm});
            skLineSegment(sketch, "E114.3.0.0", {"start": v(-3162.3, 660.4) * mm, "end": v(-3162.3, 50.8) * mm});
            skLineSegment(sketch, "E114.3.0.1", {"start": v(-3511.55, 50.8) * mm, "end": v(-3162.3, 50.8) * mm});
            skLineSegment(sketch, "E114.3.0.2", {"start": v(-3511.55, 660.4) * mm, "end": v(-3511.55, 50.8) * mm});
            skLineSegment(sketch, "E114.3.0.3", {"start": v(-3511.55, 660.4) * mm, "end": v(-3162.3, 660.4) * mm});
            skLineSegment(sketch, "E114.direction1", {"start": v(-4210.05, 50.8) * mm, "end": v(-3860.8, 50.8) * mm, "construction": true});
            skLineSegment(sketch, "E115.0", {"start": v(-4216.4, 654.05) * mm, "end": v(-4216.4, 57.15) * mm});
            skLineSegment(sketch, "E115.1", {"start": v(-4552.95, 654.05) * mm, "end": v(-4216.4, 654.05) * mm});
            skLineSegment(sketch, "E115.2", {"start": v(-4552.95, 654.05) * mm, "end": v(-4552.95, 57.15) * mm});
            skLineSegment(sketch, "E115.3", {"start": v(-4552.95, 57.15) * mm, "end": v(-4216.4, 57.15) * mm});
            skLineSegment(sketch, "E116.0", {"start": v(-4203.7, 654.05) * mm, "end": v(-3867.15, 654.05) * mm});
            skLineSegment(sketch, "E116.1", {"start": v(-4203.7, 654.05) * mm, "end": v(-4203.7, 57.15) * mm});
            skLineSegment(sketch, "E116.2", {"start": v(-4203.7, 57.15) * mm, "end": v(-3867.15, 57.15) * mm});
            skLineSegment(sketch, "E116.3", {"start": v(-3867.15, 654.05) * mm, "end": v(-3867.15, 57.15) * mm});
            skLineSegment(sketch, "E117.0", {"start": v(-3854.45, 654.05) * mm, "end": v(-3517.9, 654.05) * mm});
            skLineSegment(sketch, "E117.1", {"start": v(-3854.45, 654.05) * mm, "end": v(-3854.45, 57.15) * mm});
            skLineSegment(sketch, "E117.2", {"start": v(-3854.45, 57.15) * mm, "end": v(-3517.9, 57.15) * mm});
            skLineSegment(sketch, "E117.3", {"start": v(-3517.9, 654.05) * mm, "end": v(-3517.9, 57.15) * mm});
            skLineSegment(sketch, "E118.0", {"start": v(-3505.2, 654.05) * mm, "end": v(-3168.65, 654.05) * mm});
            skLineSegment(sketch, "E118.1", {"start": v(-3505.2, 654.05) * mm, "end": v(-3505.2, 57.15) * mm});
            skLineSegment(sketch, "E118.2", {"start": v(-3505.2, 57.15) * mm, "end": v(-3168.65, 57.15) * mm});
            skLineSegment(sketch, "E118.3", {"start": v(-3168.65, 654.05) * mm, "end": v(-3168.65, 57.15) * mm});
            skLineSegment(sketch, "E119.bottom", {"start": v(-4559.3, 2476.5) * mm, "end": v(-3162.3, 2476.5) * mm});
            skLineSegment(sketch, "E119.top", {"start": v(-4559.3, 1930.4) * mm, "end": v(-3162.3, 1930.4) * mm});
            skLineSegment(sketch, "E119.left", {"start": v(-4559.3, 2476.5) * mm, "end": v(-4559.3, 1930.4) * mm});
            skLineSegment(sketch, "E119.right", {"start": v(-3162.3, 2476.5) * mm, "end": v(-3162.3, 1930.4) * mm});
            skLineSegment(sketch, "E120.bottom", {"start": v(-4559.3, 1879.6) * mm, "end": v(-3162.3, 1879.6) * mm});
            skLineSegment(sketch, "E120.top", {"start": v(-4559.3, 1524) * mm, "end": v(-3162.3, 1524) * mm});
            skLineSegment(sketch, "E120.left", {"start": v(-4559.3, 1879.6) * mm, "end": v(-4559.3, 1524) * mm});
            skLineSegment(sketch, "E120.right", {"start": v(-3162.3, 1879.6) * mm, "end": v(-3162.3, 1524) * mm});
            skLineSegment(sketch, "E121.bottom", {"start": v(-4559.3, 1473.2) * mm, "end": v(-3162.3, 1473.2) * mm});
            skLineSegment(sketch, "E121.top", {"start": v(-4559.3, 1117.6) * mm, "end": v(-3162.3, 1117.6) * mm});
            skLineSegment(sketch, "E121.left", {"start": v(-4559.3, 1473.2) * mm, "end": v(-4559.3, 1117.6) * mm});
            skLineSegment(sketch, "E121.right", {"start": v(-3162.3, 1473.2) * mm, "end": v(-3162.3, 1117.6) * mm});
            skLineSegment(sketch, "E122.bottom", {"start": v(-4559.3, 1066.8) * mm, "end": v(-3162.3, 1066.8) * mm});
            skLineSegment(sketch, "E122.top", {"start": v(-4559.3, 711.2) * mm, "end": v(-3162.3, 711.2) * mm});
            skLineSegment(sketch, "E122.left", {"start": v(-4559.3, 1066.8) * mm, "end": v(-4559.3, 711.2) * mm});
            skLineSegment(sketch, "E122.right", {"start": v(-3162.3, 1066.8) * mm, "end": v(-3162.3, 711.2) * mm});
            skSolve(sketch);
        }
        {
            var Q0;
            Q0 = qSketchRegion(id + "F34", true);
            extrude(context, id + "F35", {"entities" : qUnion([Q0]), "operationType" : NewBodyOperationType.REMOVE, "endBound" : BoundingType.UP_TO_NEXT, "oppositeDirection" : true, "depth" : 25.4 * mm, "offsetDistance" : 25.4 * mm});
        }
        {
            var Q0;
            {var subQ4=sQuery(id+"F0.wireOp",EDGE,"E5");var subQ73=sQuery(id+"F0.wireOp",EDGE,"E0");Q0=makeQuery(id+"F8.boolean.opBoolean","SPLIT",FACE,{"disambiguationData":[TD([makeQuery(id+"F1.opExtrude","SWEPT_FACE",FACE,{"disambiguationData":[OSD([subQ4])]})])],"derivedFrom":makeQuery(id+"F1.opExtrude","SWEPT_FACE",FACE,{"disambiguationData":[OSD([subQ73])]})});}
            var sketch = newSketch(context, id + "F36", { "sketchPlane" : qUnion([Q0])});
            skLineSegment(sketch, "E123", {"start": v(-1511.3, 2527.3) * mm, "end": v(-698.5, 2527.3) * mm});
            skLineSegment(sketch, "E124", {"start": v(-698.5, 2527.3) * mm, "end": v(-698.5, 711.2) * mm});
            skLineSegment(sketch, "E125", {"start": v(-698.5, 711.2) * mm, "end": v(-12.7, 711.2) * mm});
            skLineSegment(sketch, "E126", {"start": v(-1511.3, 2527.3) * mm, "end": v(-1511.3, 0) * mm});
            skLineSegment(sketch, "E127", {"start": v(-1511.3, 0) * mm, "end": v(-12.7, 0) * mm});
            skLineSegment(sketch, "E128", {"start": v(-12.7, 0) * mm, "end": v(-12.7, 711.2) * mm});
            skLineSegment(sketch, "E129.bottom", {"start": v(-1460.5, 2476.5) * mm, "end": v(-749.3, 2476.5) * mm});
            skLineSegment(sketch, "E129.top", {"start": v(-1460.5, 1930.4) * mm, "end": v(-749.3, 1930.4) * mm});
            skLineSegment(sketch, "E129.left", {"start": v(-1460.5, 2476.5) * mm, "end": v(-1460.5, 1930.4) * mm});
            skLineSegment(sketch, "E129.right", {"start": v(-749.3, 2476.5) * mm, "end": v(-749.3, 1930.4) * mm});
            skLineSegment(sketch, "E130.bottom", {"start": v(-1460.5, 1879.6) * mm, "end": v(-749.3, 1879.6) * mm});
            skLineSegment(sketch, "E130.top", {"start": v(-1460.5, 1524) * mm, "end": v(-749.3, 1524) * mm});
            skLineSegment(sketch, "E130.left", {"start": v(-1460.5, 1879.6) * mm, "end": v(-1460.5, 1524) * mm});
            skLineSegment(sketch, "E130.right", {"start": v(-749.3, 1879.6) * mm, "end": v(-749.3, 1524) * mm});
            skLineSegment(sketch, "E131.bottom", {"start": v(-1460.5, 1473.2) * mm, "end": v(-749.3, 1473.2) * mm});
            skLineSegment(sketch, "E131.top", {"start": v(-1460.5, 1117.6) * mm, "end": v(-749.3, 1117.6) * mm});
            skLineSegment(sketch, "E131.left", {"start": v(-1460.5, 1473.2) * mm, "end": v(-1460.5, 1117.6) * mm});
            skLineSegment(sketch, "E131.right", {"start": v(-749.3, 1473.2) * mm, "end": v(-749.3, 1117.6) * mm});
            skLineSegment(sketch, "E132.bottom", {"start": v(-1460.5, 1066.8) * mm, "end": v(-749.3, 1066.8) * mm});
            skLineSegment(sketch, "E132.top", {"start": v(-1460.5, 711.2) * mm, "end": v(-749.3, 711.2) * mm});
            skLineSegment(sketch, "E132.left", {"start": v(-1460.5, 1066.8) * mm, "end": v(-1460.5, 711.2) * mm});
            skLineSegment(sketch, "E132.right", {"start": v(-749.3, 1066.8) * mm, "end": v(-749.3, 711.2) * mm});
            skSolve(sketch);
        }
        {
            var Q0;
            Q0 = qSketchRegion(id + "F36", true);
            var Q1;
            Q1=makeQuery(id+"F8.opExtrude","SWEPT_FACE",FACE,{"disambiguationData":[OSD([sQuery(id+"F7.wireOp",EDGE,"E85")])]});
            extrude(context, id + "F37", {"entities" : qUnion([Q0]), "operationType" : NewBodyOperationType.ADD, "endBound" : BoundingType.UP_TO_SURFACE, "depth" : 25.4 * mm, "endBoundEntityFace" : qUnion([Q1]), "offsetDistance" : 25.4 * mm});
        }
        {
            var Q0;
            Q0=makeQuery(id+"F37.opExtrude","CAP_FACE",FACE,{"disambiguationData":[OSD([sQuery(id+"F36.wireOp",EDGE,"E123"),sQuery(id+"F36.wireOp",EDGE,"E124"),sQuery(id+"F36.wireOp",EDGE,"E125"),sQuery(id+"F36.wireOp",EDGE,"E126"),sQuery(id+"F36.wireOp",EDGE,"E127"),sQuery(id+"F36.wireOp",EDGE,"E128"),sQuery(id+"F36.wireOp",EDGE,"E129.bottom"),sQuery(id+"F36.wireOp",EDGE,"E129.top"),sQuery(id+"F36.wireOp",EDGE,"E129.left"),sQuery(id+"F36.wireOp",EDGE,"E129.right"),sQuery(id+"F36.wireOp",EDGE,"E130.bottom"),sQuery(id+"F36.wireOp",EDGE,"E130.top"),sQuery(id+"F36.wireOp",EDGE,"E130.left"),sQuery(id+"F36.wireOp",EDGE,"E130.right"),sQuery(id+"F36.wireOp",EDGE,"E131.bottom"),sQuery(id+"F36.wireOp",EDGE,"E131.top"),sQuery(id+"F36.wireOp",EDGE,"E131.left"),sQuery(id+"F36.wireOp",EDGE,"E131.right"),sQuery(id+"F36.wireOp",EDGE,"E132.bottom"),sQuery(id+"F36.wireOp",EDGE,"E132.top"),sQuery(id+"F36.wireOp",EDGE,"E132.left"),sQuery(id+"F36.wireOp",EDGE,"E132.right")])],"isStart":false});
            var sketch = newSketch(context, id + "F38", { "sketchPlane" : qUnion([Q0])});
            skLineSegment(sketch, "E133.bottom", {"start": v(-698.5, 660.4) * mm, "end": v(-63.5, 660.4) * mm});
            skLineSegment(sketch, "E133.top", {"start": v(-698.5, 381) * mm, "end": v(-63.5, 381) * mm});
            skLineSegment(sketch, "E133.left", {"start": v(-698.5, 660.4) * mm, "end": v(-698.5, 381) * mm});
            skLineSegment(sketch, "E133.right", {"start": v(-63.5, 660.4) * mm, "end": v(-63.5, 381) * mm});
            skLineSegment(sketch, "E134.bottom", {"start": v(-698.5, 330.2) * mm, "end": v(-63.5, 330.2) * mm});
            skLineSegment(sketch, "E134.top", {"start": v(-698.5, 50.8) * mm, "end": v(-63.5, 50.8) * mm});
            skLineSegment(sketch, "E134.left", {"start": v(-698.5, 330.2) * mm, "end": v(-698.5, 50.8) * mm});
            skLineSegment(sketch, "E134.right", {"start": v(-63.5, 330.2) * mm, "end": v(-63.5, 50.8) * mm});
            skLineSegment(sketch, "E135.bottom", {"start": v(-1460.5, 660.4) * mm, "end": v(-1104.9, 660.4) * mm});
            skLineSegment(sketch, "E135.top", {"start": v(-1460.5, 50.8) * mm, "end": v(-1104.9, 50.8) * mm});
            skLineSegment(sketch, "E135.left", {"start": v(-1460.5, 660.4) * mm, "end": v(-1460.5, 50.8) * mm});
            skLineSegment(sketch, "E135.right", {"start": v(-1104.9, 660.4) * mm, "end": v(-1104.9, 50.8) * mm});
            skLineSegment(sketch, "E136.bottom", {"start": v(-1104.9, 660.4) * mm, "end": v(-749.3, 660.4) * mm});
            skLineSegment(sketch, "E136.top", {"start": v(-1104.9, 50.8) * mm, "end": v(-749.3, 50.8) * mm});
            skLineSegment(sketch, "E136.right", {"start": v(-749.3, 660.4) * mm, "end": v(-749.3, 50.8) * mm});
            skLineSegment(sketch, "E137.0", {"start": v(-1454.15, 654.05) * mm, "end": v(-1111.25, 654.05) * mm});
            skLineSegment(sketch, "E137.1", {"start": v(-1454.15, 654.05) * mm, "end": v(-1454.15, 57.15) * mm});
            skLineSegment(sketch, "E137.2", {"start": v(-1454.15, 57.15) * mm, "end": v(-1111.25, 57.15) * mm});
            skLineSegment(sketch, "E137.3", {"start": v(-1111.25, 654.05) * mm, "end": v(-1111.25, 57.15) * mm});
            skLineSegment(sketch, "E138.0", {"start": v(-1098.55, 654.05) * mm, "end": v(-755.65, 654.05) * mm});
            skLineSegment(sketch, "E138.1", {"start": v(-1098.55, 654.05) * mm, "end": v(-1098.55, 57.15) * mm});
            skLineSegment(sketch, "E138.2", {"start": v(-1098.55, 57.15) * mm, "end": v(-755.65, 57.15) * mm});
            skLineSegment(sketch, "E138.3", {"start": v(-755.65, 654.05) * mm, "end": v(-755.65, 57.15) * mm});
            skSolve(sketch);
        }
        {
            var Q0;
            Q0 = qSketchRegion(id + "F38", true);
            extrude(context, id + "F39", {"entities" : qUnion([Q0]), "operationType" : NewBodyOperationType.REMOVE, "endBound" : BoundingType.UP_TO_NEXT, "oppositeDirection" : true, "depth" : 25.4 * mm, "offsetDistance" : 25.4 * mm});
        }
        {
            var Q0;
            Q0=makeQuery(id+"F4.boolean.opBoolean","MERGE",FACE,{"derivedFrom":[makeQuery(id+"F1.opExtrude","SWEPT_FACE",FACE,{"disambiguationData":[OSD([sQuery(id+"F0.wireOp",EDGE,"E11")])]})],"fromTools":[makeQuery(id+"F4.opExtrude","SWEPT_FACE",FACE,{"disambiguationData":[OSD([sQuery(id+"F3.wireOp",EDGE,"E82.bottom")])]})]});
            var sketch = newSketch(context, id + "F40", { "sketchPlane" : qUnion([Q0])});
            skLineSegment(sketch, "E139.bottom", {"start": v(-6146.8, 2032) * mm, "end": v(-4025.9, 2032) * mm});
            skLineSegment(sketch, "E139.top", {"start": v(-6146.8, 1257.3) * mm, "end": v(-4025.9, 1257.3) * mm});
            skLineSegment(sketch, "E139.left", {"start": v(-6146.8, 2032) * mm, "end": v(-6146.8, 1257.3) * mm});
            skLineSegment(sketch, "E139.right", {"start": v(-4025.9, 2032) * mm, "end": v(-4025.9, 1257.3) * mm});
            skSolve(sketch);
        }
        {
            var Q0;
            Q0 = qSketchRegion(id + "F40", true);
            extrude(context, id + "F41", {"entities" : qUnion([Q0]), "operationType" : NewBodyOperationType.REMOVE, "endBound" : BoundingType.UP_TO_NEXT, "oppositeDirection" : true, "depth" : 25.4 * mm, "offsetDistance" : 25.4 * mm});
        }
        {
            var Q0;
            Q0=qCreatedBy(makeId("Top.planeOp"),FACE);
            var sketch = newSketch(context, id + "F42", { "sketchPlane" : qUnion([Q0])});
            skLineSegment(sketch, "E140.bottom", {"start": v(3403.6, 4572) * mm, "end": v(5842, 4572) * mm});
            skLineSegment(sketch, "E140.top", {"start": v(3403.6, 3683) * mm, "end": v(5842, 3683) * mm});
            skLineSegment(sketch, "E140.left", {"start": v(3403.6, 4572) * mm, "end": v(3403.6, 3683) * mm});
            skLineSegment(sketch, "E140.right", {"start": v(5842, 4572) * mm, "end": v(5842, 3683) * mm});
            skSolve(sketch);
        }
        {
            var Q0;
            Q0 = qSketchRegion(id + "F42", true);
            extrude(context, id + "F43", {"entities" : qUnion([Q0]), "depth" : 857.25 * mm, "offsetDistance" : 25.4 * mm});
        }
        {
            var Q0;
            Q0=makeQuery(id+"F43.opExtrude","SWEPT_FACE",FACE,{"disambiguationData":[OSD([sQuery(id+"F42.wireOp",EDGE,"E140.top")])]});
            var sketch = newSketch(context, id + "F44", { "sketchPlane" : qUnion([Q0])});
            skLineSegment(sketch, "E141", {"start": v(3403.6, 609.6) * mm, "end": v(3606.8, 609.6) * mm});
            skLineSegment(sketch, "E142", {"start": v(3606.8, 609.6) * mm, "end": v(3606.8, 457.2) * mm});
            skLineSegment(sketch, "E143", {"start": v(3606.8, 457.2) * mm, "end": v(5638.8, 457.2) * mm});
            skLineSegment(sketch, "E144", {"start": v(5638.8, 457.2) * mm, "end": v(5638.8, 609.6) * mm});
            skLineSegment(sketch, "E145", {"start": v(5638.8, 609.6) * mm, "end": v(5842, 609.6) * mm});
            skLineSegment(sketch, "E146", {"start": v(3403.6, 609.6) * mm, "end": v(3403.6, 857.25) * mm});
            skLineSegment(sketch, "E147", {"start": v(3403.6, 857.25) * mm, "end": v(5842, 857.25) * mm});
            skLineSegment(sketch, "E148", {"start": v(5842, 857.25) * mm, "end": v(5842, 609.6) * mm});
            skSolve(sketch);
        }
        {
            var Q0;
            Q0 = qSketchRegion(id + "F44", true);
            extrude(context, id + "F45", {"entities" : qUnion([Q0]), "operationType" : NewBodyOperationType.REMOVE, "oppositeDirection" : true, "depth" : 591.82 * mm, "offsetDistance" : 25.4 * mm});
        }
        {
            var Q0;
            Q0=qCreatedBy(makeId("Top.planeOp"),FACE);
            var sketch = newSketch(context, id + "F46", { "sketchPlane" : qUnion([Q0])});
            skLineSegment(sketch, "E149.bottom", {"start": v(2357.95, 3581.09) * mm, "end": v(3278.7, 3581.09) * mm});
            skLineSegment(sketch, "E149.top", {"start": v(2357.95, 1860.24) * mm, "end": v(3278.7, 1860.24) * mm});
            skLineSegment(sketch, "E149.left", {"start": v(2357.95, 3581.09) * mm, "end": v(2357.95, 1860.24) * mm});
            skLineSegment(sketch, "E149.right", {"start": v(3278.7, 3581.09) * mm, "end": v(3278.7, 1860.24) * mm});
            skSolve(sketch);
        }
        {
            var Q0;
            Q0=makeQuery(id+"F46.imprint","IMPRINT",FACE,{"disambiguationData":[TD([[makeQuery(id+"F46.imprint","IMPRINT",EDGE,{"derivedFrom":sQuery(id+"F46.wireOp",EDGE,"E149.bottom")}),-1.0]])]});
            extrude(context, id + "F47", {"entities" : qUnion([Q0]), "depth" : 793.75 * mm, "offsetDistance" : 25.4 * mm});
        }
        {
            var Q0;
            Q0=makeQuery(id+"F47.opExtrude","SWEPT_FACE",FACE,{"disambiguationData":[OSD([sQuery(id+"F46.wireOp",EDGE,"E149.right")])]});
            var sketch = newSketch(context, id + "F48", { "sketchPlane" : qUnion([Q0])});
            skLineSegment(sketch, "E150", {"start": v(1860.24, 584.2) * mm, "end": v(2063.44, 584.2) * mm});
            skLineSegment(sketch, "E151", {"start": v(2063.44, 584.2) * mm, "end": v(2063.44, 406.4) * mm});
            skLineSegment(sketch, "E152", {"start": v(2063.44, 406.4) * mm, "end": v(3377.89, 406.4) * mm});
            skLineSegment(sketch, "E153", {"start": v(3377.89, 406.4) * mm, "end": v(3377.89, 584.2) * mm});
            skLineSegment(sketch, "E154", {"start": v(3377.89, 584.2) * mm, "end": v(3581.09, 584.2) * mm});
            skLineSegment(sketch, "E155", {"start": v(3581.09, 584.2) * mm, "end": v(3581.09, 793.75) * mm});
            skLineSegment(sketch, "E156", {"start": v(3581.09, 793.75) * mm, "end": v(1860.24, 793.75) * mm});
            skLineSegment(sketch, "E157", {"start": v(1860.24, 793.75) * mm, "end": v(1860.24, 584.2) * mm});
            skSolve(sketch);
        }
        {
            var Q0;
            Q0 = qSketchRegion(id + "F48", true);
            extrude(context, id + "F49", {"entities" : qUnion([Q0]), "operationType" : NewBodyOperationType.REMOVE, "oppositeDirection" : true, "depth" : 711.2 * mm, "offsetDistance" : 25.4 * mm});
        }
        {
            var Q0;
            Q0=qCreatedBy(makeId("Top.planeOp"),FACE);
            var sketch = newSketch(context, id + "F50", { "sketchPlane" : qUnion([Q0])});
            skLineSegment(sketch, "E158", {"start": v(3909.88, 1324.6) * mm, "end": v(3383.85, 747.25) * mm});
            skLineSegment(sketch, "E159", {"start": v(3383.85, 747.25) * mm, "end": v(4017.52, 169.9) * mm});
            skLineSegment(sketch, "E160", {"start": v(4017.52, 169.9) * mm, "end": v(4543.55, 747.25) * mm});
            skLineSegment(sketch, "E161", {"start": v(4543.55, 747.25) * mm, "end": v(3909.88, 1324.6) * mm});
            skLineSegment(sketch, "E162", {"start": v(5968.44, 854.9) * mm, "end": v(5391.1, 1380.92) * mm});
            skLineSegment(sketch, "E163", {"start": v(5391.1, 1380.92) * mm, "end": v(4813.74, 747.25) * mm});
            skLineSegment(sketch, "E164", {"start": v(4813.74, 747.25) * mm, "end": v(5391.1, 221.22) * mm});
            skLineSegment(sketch, "E165", {"start": v(5391.1, 221.22) * mm, "end": v(5968.44, 854.9) * mm});
            skSolve(sketch);
        }
        {
            var Q0;
            Q0 = qSketchRegion(id + "F50", true);
            extrude(context, id + "F51", {"entities" : qUnion([Q0]), "depth" : 1047.75 * mm, "offsetDistance" : 25.4 * mm});
        }
        {
            var Q0;
            Q0=makeQuery(id+"F51.opExtrude","SWEPT_FACE",FACE,{"disambiguationData":[OSD([sQuery(id+"F50.wireOp",EDGE,"E163")])]});
            var sketch = newSketch(context, id + "F52", { "sketchPlane" : qUnion([Q0])});
            skLineSegment(sketch, "E166", {"start": v(-4651.62, 609.6) * mm, "end": v(-4473.82, 609.6) * mm});
            skLineSegment(sketch, "E167", {"start": v(-4473.82, 609.6) * mm, "end": v(-4473.82, 431.8) * mm});
            skLineSegment(sketch, "E168", {"start": v(-4473.82, 431.8) * mm, "end": v(-3972.17, 431.8) * mm});
            skLineSegment(sketch, "E169", {"start": v(-3972.17, 431.8) * mm, "end": v(-3972.17, 609.6) * mm});
            skLineSegment(sketch, "E170", {"start": v(-3972.17, 609.6) * mm, "end": v(-3794.37, 609.6) * mm});
            skLineSegment(sketch, "E171", {"start": v(-3794.37, 609.6) * mm, "end": v(-3794.37, 1047.75) * mm});
            skLineSegment(sketch, "E172", {"start": v(-3794.37, 1047.75) * mm, "end": v(-4651.62, 1047.75) * mm});
            skLineSegment(sketch, "E173", {"start": v(-4651.62, 1047.75) * mm, "end": v(-4651.62, 609.6) * mm});
            skSolve(sketch);
        }
        {
            var Q0;
            Q0 = qSketchRegion(id + "F52", true);
            extrude(context, id + "F53", {"entities" : qUnion([Q0]), "operationType" : NewBodyOperationType.REMOVE, "oppositeDirection" : true, "depth" : 553.72 * mm, "offsetDistance" : 25.4 * mm});
        }
        {
            var Q0;
            Q0=makeQuery(id+"F51.opExtrude","SWEPT_BODY",BODY,{"disambiguationData":[OSD([sQuery(id+"F50.wireOp",EDGE,"E158"),sQuery(id+"F50.wireOp",EDGE,"E159"),sQuery(id+"F50.wireOp",EDGE,"E160"),sQuery(id+"F50.wireOp",EDGE,"E161")])]});
            deleteBodies(context, id + "F54", {"entities" : qUnion([Q0])});
        }
        {
            var Q0;
            Q0=makeQuery(id+"F51.opExtrude","SWEPT_BODY",BODY,{"disambiguationData":[OSD([sQuery(id+"F50.wireOp",EDGE,"E162"),sQuery(id+"F50.wireOp",EDGE,"E163"),sQuery(id+"F50.wireOp",EDGE,"E164"),sQuery(id+"F50.wireOp",EDGE,"E165")])]});
            var Q1;
            Q1=makeQuery(id+"F1.opExtrude","SWEPT_EDGE",EDGE,{"disambiguationData":[OSD([sQuery(id+"F0.wireOp",EDGE,"E3"),sQuery(id+"F0.wireOp",EDGE,"E4")])]});
            transform(context, id + "F55", {"entities" : qUnion([Q0]), "transformType" : TransformType.ROTATION, "transformAxis" : qUnion([Q1]), "angle" : 90 * degree, "makeCopy" : true});
        }
        {
            var Q0;
            Q0=makeQuery(id+"F55.opPattern","COPY",BODY,{"derivedFrom":makeQuery(id+"F51.opExtrude","SWEPT_BODY",BODY,{"disambiguationData":[OSD([sQuery(id+"F50.wireOp",EDGE,"E162"),sQuery(id+"F50.wireOp",EDGE,"E163"),sQuery(id+"F50.wireOp",EDGE,"E164"),sQuery(id+"F50.wireOp",EDGE,"E165")])]}),"instanceName":"1"});
            transform(context, id + "F56", {"entities" : qUnion([Q0]), "transformType" : TransformType.TRANSLATION_3D, "dx" : 0 * mm, "dy" : 2486.66 * mm, "dz" : 0 * mm, "makeCopy" : false});
        }
    });
